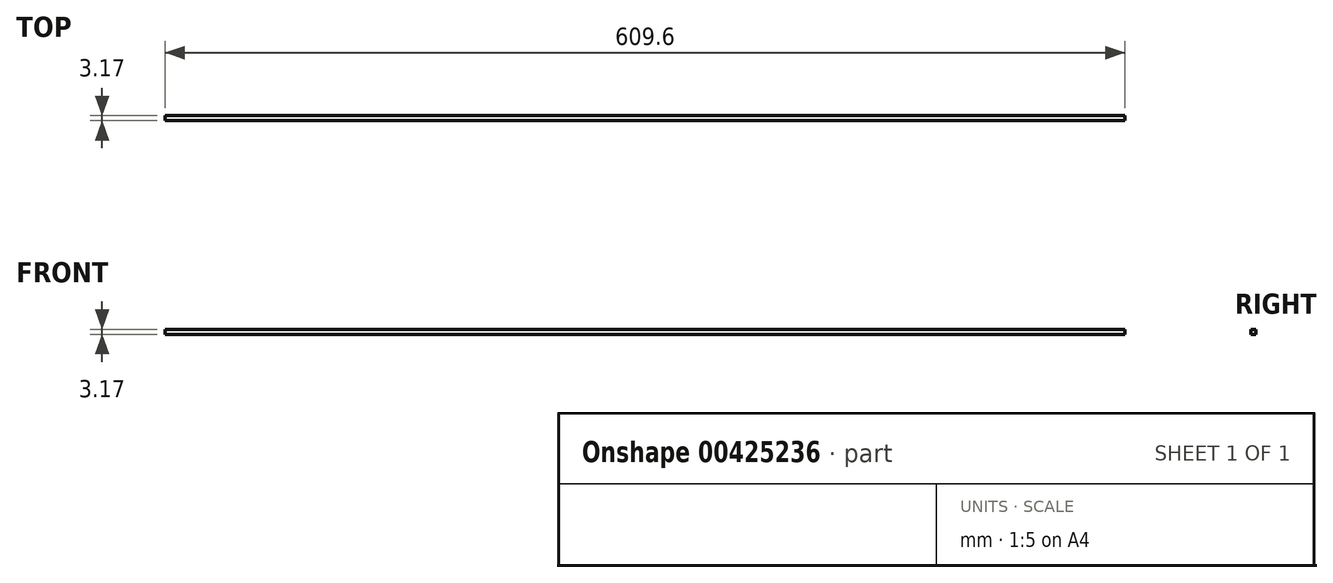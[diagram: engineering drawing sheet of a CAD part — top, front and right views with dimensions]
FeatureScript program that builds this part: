
annotation { "Feature Type Name" : "Feature", "Feature Type Description" : "" }
export const myFeature = defineFeature(function(context is Context, id is Id, definition is map)
    precondition{}
    {
        {
            var Q0;
            Q0=qCreatedBy(makeId("Front.planeOp"),FACE);
            var sketch = newSketch(context, id + "F0", { "sketchPlane" : qUnion([Q0])});
            skLineSegment(sketch, "E0.bottom", {"start": v(-299.74, 17.67) * mm, "end": v(309.86, 17.67) * mm});
            skLineSegment(sketch, "E0.top", {"start": v(-299.74, 14.5) * mm, "end": v(309.86, 14.5) * mm});
            skLineSegment(sketch, "E0.left", {"start": v(-299.74, 17.67) * mm, "end": v(-299.74, 14.5) * mm});
            skLineSegment(sketch, "E0.right", {"start": v(309.86, 17.67) * mm, "end": v(309.86, 14.5) * mm});
            skSolve(sketch);
        }
        {
            var Q0;
            Q0=makeQuery(id+"F0.imprint","IMPRINT",FACE,{"disambiguationData":[TD([[makeQuery(id+"F0.imprint","IMPRINT",EDGE,{"derivedFrom":sQuery(id+"F0.wireOp",EDGE,"E0.bottom")}),-1.0]])]});
            extrude(context, id + "F1", {"entities" : qUnion([Q0]), "depth" : 3.17 * mm});
        }
    });
